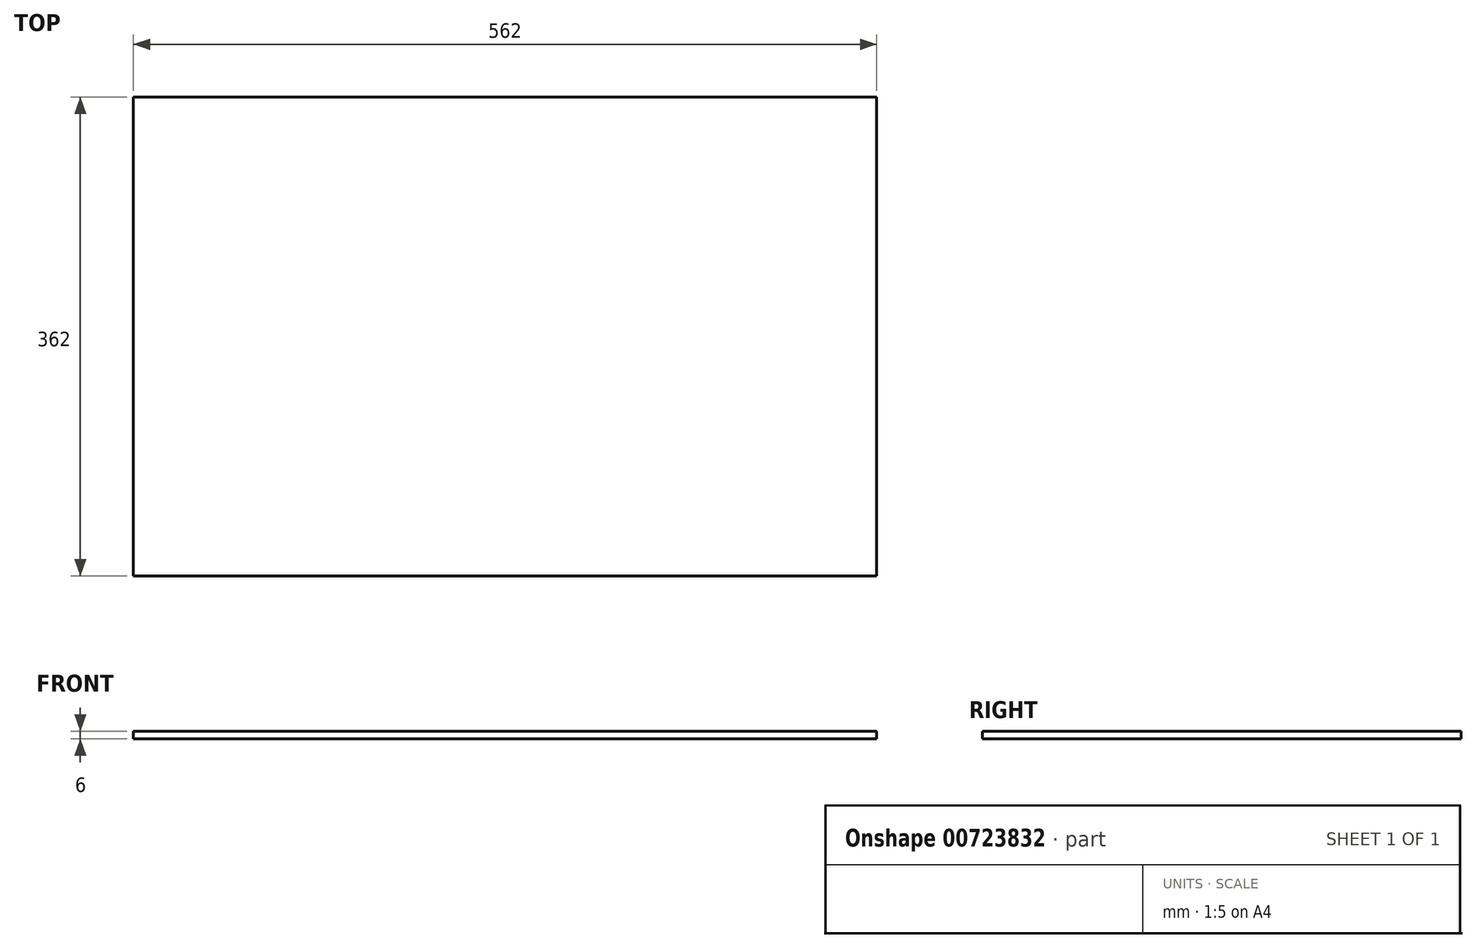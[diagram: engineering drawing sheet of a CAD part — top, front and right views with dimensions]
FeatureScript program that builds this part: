
annotation { "Feature Type Name" : "Feature", "Feature Type Description" : "" }
export const myFeature = defineFeature(function(context is Context, id is Id, definition is map)
    precondition{}
    {
        {
            var Q0;
            Q0=qCreatedBy(makeId("Top.planeOp"),FACE);
            var sketch = newSketch(context, id + "F0", { "sketchPlane" : qUnion([Q0])});
            skLineSegment(sketch, "E0.bottom", {"start": v(281, 181) * mm, "end": v(-281, 181) * mm});
            skLineSegment(sketch, "E0.top", {"start": v(281, -181) * mm, "end": v(-281, -181) * mm});
            skLineSegment(sketch, "E0.left", {"start": v(281, 181) * mm, "end": v(281, -181) * mm});
            skLineSegment(sketch, "E0.right", {"start": v(-281, 181) * mm, "end": v(-281, -181) * mm});
            skPoint(sketch, "E0.middle", {"position": v(0, 0) * mm});
            skSolve(sketch);
        }
        {
            var Q0;
            Q0=makeQuery(id+"F0.imprint","IMPRINT",FACE,{"disambiguationData":[TD([[makeQuery(id+"F0.imprint","IMPRINT",EDGE,{"derivedFrom":sQuery(id+"F0.wireOp",EDGE,"E0.bottom")}),1.0]])]});
            extrude(context, id + "F1", {"entities" : qUnion([Q0]), "depth" : 6 * mm, "offsetDistance" : 25 * mm});
        }
    });
